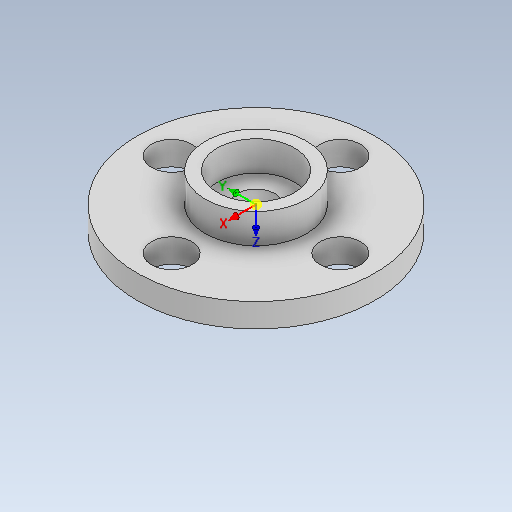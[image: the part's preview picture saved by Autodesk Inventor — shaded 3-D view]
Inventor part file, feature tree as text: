
AUTODESK INVENTOR PART (.ipt)
format: ipt  version: 2020 (Build 240168000, 168)  size: 157,184 bytes
history: native  units: mm
features: other x2, extrude x2, sketch x2
ambient origin geometry x8: Origin, YZ Plane, XZ Plane, XY Plane, X Axis, Y Axis, Z Axis, Center Point
bodies: Body1 (feature_tree)
feature tree (6):
  other  "С поворотом:10"
  other  "Твердое тело1"
  extrude  "Выдавливание1"  Depth=20.0mm
  extrude  "Выдавливание2"  Depth=3.2mm
  sketch  "Эскиз1"
  sketch  "Эскиз2"
